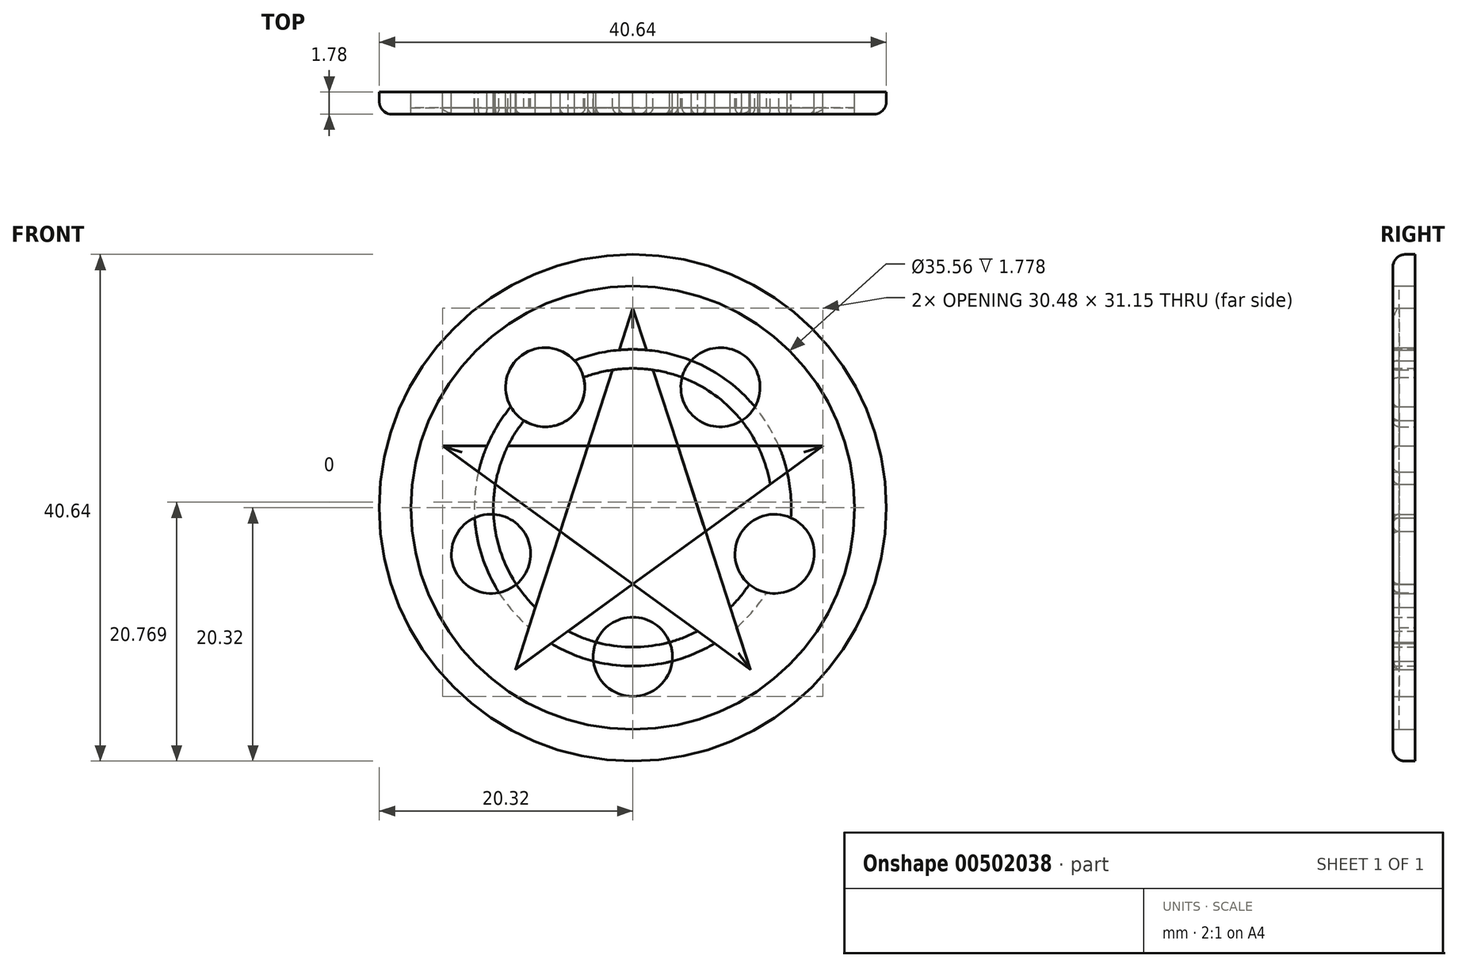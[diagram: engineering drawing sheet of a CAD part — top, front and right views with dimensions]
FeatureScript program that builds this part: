
annotation { "Feature Type Name" : "Feature", "Feature Type Description" : "" }
export const myFeature = defineFeature(function(context is Context, id is Id, definition is map)
    precondition{}
    {
        {
            var Q0;
            Q0=qCreatedBy(makeId("Front.planeOp"),FACE);
            var sketch = newSketch(context, id + "F0", { "sketchPlane" : qUnion([Q0])});
            skCircle(sketch, "E0", {"center": v(0, 0) * mm, "radius": 20.32 * mm});
            skCircle(sketch, "E1", {"center": v(0, 0) * mm, "radius": 17.78 * mm});
            skLineSegment(sketch, "E2", {"start": v(0, 16.02) * mm, "end": v(-9.42, -12.96) * mm});
            skLineSegment(sketch, "E3", {"start": v(-9.42, -12.96) * mm, "end": v(15.24, 4.95) * mm});
            skLineSegment(sketch, "E4", {"start": v(-15.24, 4.95) * mm, "end": v(15.24, 4.95) * mm});
            skLineSegment(sketch, "E5", {"start": v(0, 16.02) * mm, "end": v(9.42, -12.96) * mm});
            skLineSegment(sketch, "E6", {"start": v(9.42, -12.96) * mm, "end": v(-15.24, 4.95) * mm});
            skPoint(sketch, "E7", {"position": v(3.6, 4.95) * mm});
            skPoint(sketch, "E8", {"position": v(-3.6, 4.95) * mm});
            skPoint(sketch, "E9", {"position": v(-5.82, -1.9) * mm});
            skPoint(sketch, "E10", {"position": v(0, -6.12) * mm});
            skPoint(sketch, "E11", {"position": v(5.82, -1.9) * mm});
            skPoint(sketch, "E12", {"position": v(-7.02, 9.67) * mm});
            skPoint(sketch, "E13", {"position": v(7.02, 9.67) * mm});
            skPoint(sketch, "E14", {"position": v(11.37, -3.7) * mm});
            skPoint(sketch, "E15", {"position": v(0, -11.95) * mm});
            skPoint(sketch, "E16", {"position": v(-11.37, -3.7) * mm});
            skPoint(sketch, "E17.orphan", {"position": v(-10.45, 14.38) * mm});
            skPoint(sketch, "E18.end.orphan", {"position": v(10.45, 14.38) * mm});
            skPoint(sketch, "E19.end.orphan", {"position": v(16.9, -5.5) * mm});
            skPoint(sketch, "E20.end.orphan", {"position": v(0, -17.78) * mm});
            skPoint(sketch, "E21.end.orphan", {"position": v(-16.9, -5.5) * mm});
            skCircle(sketch, "E22", {"center": v(-7.02, 9.67) * mm, "radius": 3.18 * mm});
            skCircle(sketch, "E23", {"center": v(-11.37, -3.7) * mm, "radius": 3.18 * mm});
            skCircle(sketch, "E24", {"center": v(0, -11.95) * mm, "radius": 3.18 * mm});
            skCircle(sketch, "E25", {"center": v(11.37, -3.7) * mm, "radius": 3.18 * mm});
            skCircle(sketch, "E26", {"center": v(7.02, 9.67) * mm, "radius": 3.18 * mm});
            skCircle(sketch, "E27", {"center": v(0, 0) * mm, "radius": 12.7 * mm});
            skCircle(sketch, "E28", {"center": v(0, 0) * mm, "radius": 11.18 * mm});
            skSolve(sketch);
        }
        {
            var Q0;
            Q0=makeQuery(id+"F0.imprint","IMPRINT",FACE,{"disambiguationData":[TD([[makeQuery(id+"F0.imprint","IMPRINT",EDGE,{"derivedFrom":sQuery(id+"F0.wireOp",EDGE,"E0")}),1.0]])]});
            var Q1;
            {var subQ0=sQuery(id+"F0.wireOp",EDGE,"E4");var subQ1=sQuery(id+"F0.wireOp",EDGE,"E2");var subQ2=makeQuery(id+"F0.imprint","INTERSECT",VERTEX,{"derivedFrom":[subQ1,subQ0]});Q1=makeQuery(id+"F0.imprint","IMPRINT",FACE,{"disambiguationData":[TD([[makeQuery(id+"F0.imprint","IMPRINT",EDGE,{"disambiguationData":[TD([[subQ2,-1.0]])],"derivedFrom":subQ1}),-1.0]])]});}
            var Q2;
            {var subQ0=sQuery(id+"F0.wireOp",EDGE,"E5");var subQ1=sQuery(id+"F0.wireOp",EDGE,"E2");var subQ2=makeQuery(id+"F0.imprint","INTERSECT",VERTEX,{"derivedFrom":[subQ1,subQ0]});Q2=makeQuery(id+"F0.imprint","IMPRINT",FACE,{"disambiguationData":[TD([[makeQuery(id+"F0.imprint","IMPRINT",EDGE,{"disambiguationData":[TD([[subQ2,-1.0]])],"derivedFrom":subQ1}),1.0]])]});}
            var Q3;
            {var subQ0=sQuery(id+"F0.wireOp",EDGE,"E4");var subQ1=sQuery(id+"F0.wireOp",EDGE,"E3");var subQ2=makeQuery(id+"F0.imprint","INTERSECT",VERTEX,{"derivedFrom":[subQ1,subQ0]});Q3=makeQuery(id+"F0.imprint","IMPRINT",FACE,{"disambiguationData":[TD([[makeQuery(id+"F0.imprint","IMPRINT",EDGE,{"disambiguationData":[TD([[subQ2,1.0]])],"derivedFrom":subQ1}),1.0]])]});}
            var Q4;
            {var subQ0=sQuery(id+"F0.wireOp",EDGE,"E6");var subQ1=sQuery(id+"F0.wireOp",EDGE,"E3");var subQ2=makeQuery(id+"F0.imprint","INTERSECT",VERTEX,{"derivedFrom":[subQ1,subQ0]});Q4=makeQuery(id+"F0.imprint","IMPRINT",FACE,{"disambiguationData":[TD([[makeQuery(id+"F0.imprint","IMPRINT",EDGE,{"disambiguationData":[TD([[subQ2,-1.0]])],"derivedFrom":subQ1}),-1.0]])]});}
            var Q5;
            {var subQ0=sQuery(id+"F0.wireOp",EDGE,"E3");var subQ1=sQuery(id+"F0.wireOp",EDGE,"E2");var subQ2=makeQuery(id+"F0.imprint","INTERSECT",VERTEX,{"derivedFrom":[subQ1,subQ0]});Q5=makeQuery(id+"F0.imprint","IMPRINT",FACE,{"disambiguationData":[TD([[makeQuery(id+"F0.imprint","IMPRINT",EDGE,{"disambiguationData":[TD([[subQ2,1.0]])],"derivedFrom":subQ1}),1.0]])]});}
            var Q6;
            Q6=makeQuery(id+"F0.imprint","IMPRINT",FACE,{"disambiguationData":[TD([[makeQuery(id+"F0.imprint","IMPRINT",EDGE,{"derivedFrom":sQuery(id+"F0.wireOp",EDGE,"E23")}),1.0]])]});
            var Q7;
            Q7=makeQuery(id+"F0.imprint","IMPRINT",FACE,{"disambiguationData":[TD([[makeQuery(id+"F0.imprint","IMPRINT",EDGE,{"derivedFrom":sQuery(id+"F0.wireOp",EDGE,"E22")}),1.0]])]});
            var Q8;
            Q8=makeQuery(id+"F0.imprint","IMPRINT",FACE,{"disambiguationData":[TD([[makeQuery(id+"F0.imprint","IMPRINT",EDGE,{"derivedFrom":sQuery(id+"F0.wireOp",EDGE,"E26")}),1.0]])]});
            var Q9;
            Q9=makeQuery(id+"F0.imprint","IMPRINT",FACE,{"disambiguationData":[TD([[makeQuery(id+"F0.imprint","IMPRINT",EDGE,{"derivedFrom":sQuery(id+"F0.wireOp",EDGE,"E25")}),1.0]])]});
            var Q10;
            Q10=makeQuery(id+"F0.imprint","IMPRINT",FACE,{"disambiguationData":[TD([[makeQuery(id+"F0.imprint","IMPRINT",EDGE,{"derivedFrom":sQuery(id+"F0.wireOp",EDGE,"E24")}),1.0]])]});
            var Q11;
            {var subQ0=sQuery(id+"F0.wireOp",EDGE,"E28");var subQ1=sQuery(id+"F0.wireOp",EDGE,"E2");var subQ2=makeQuery(id+"F0.imprint","INTERSECT",VERTEX,{"disambiguationData":[OD(0.0)],"derivedFrom":[subQ1,subQ0]});Q11=makeQuery(id+"F0.imprint","IMPRINT",FACE,{"disambiguationData":[TD([[makeQuery(id+"F0.imprint","IMPRINT",EDGE,{"disambiguationData":[TD([[subQ2,-1.0]])],"derivedFrom":subQ1}),1.0]])]});}
            var Q12;
            {var subQ0=sQuery(id+"F0.wireOp",EDGE,"E27");var subQ1=sQuery(id+"F0.wireOp",EDGE,"E2");var subQ2=makeQuery(id+"F0.imprint","INTERSECT",VERTEX,{"disambiguationData":[OD(0.0)],"derivedFrom":[subQ1,subQ0]});Q12=makeQuery(id+"F0.imprint","IMPRINT",FACE,{"disambiguationData":[TD([[makeQuery(id+"F0.imprint","IMPRINT",EDGE,{"disambiguationData":[TD([[subQ2,-1.0]])],"derivedFrom":subQ1}),1.0]])]});}
            var Q13;
            {var subQ0=sQuery(id+"F0.wireOp",EDGE,"E5");var subQ1=sQuery(id+"F0.wireOp",EDGE,"E3");var subQ2=makeQuery(id+"F0.imprint","INTERSECT",VERTEX,{"derivedFrom":[subQ1,subQ0]});Q13=makeQuery(id+"F0.imprint","IMPRINT",FACE,{"disambiguationData":[TD([[makeQuery(id+"F0.imprint","IMPRINT",EDGE,{"disambiguationData":[TD([[subQ2,-1.0]])],"derivedFrom":subQ1}),1.0]])]});}
            var Q14;
            {var subQ0=sQuery(id+"F0.wireOp",EDGE,"E28");var subQ1=sQuery(id+"F0.wireOp",EDGE,"E3");var subQ2=makeQuery(id+"F0.imprint","INTERSECT",VERTEX,{"disambiguationData":[OD(1.0)],"derivedFrom":[subQ1,subQ0]});Q14=makeQuery(id+"F0.imprint","IMPRINT",FACE,{"disambiguationData":[TD([[makeQuery(id+"F0.imprint","IMPRINT",EDGE,{"disambiguationData":[TD([[subQ2,-1.0]])],"derivedFrom":subQ1}),1.0]])]});}
            var Q15;
            {var subQ0=sQuery(id+"F0.wireOp",EDGE,"E6");var subQ1=sQuery(id+"F0.wireOp",EDGE,"E5");var subQ2=makeQuery(id+"F0.imprint","INTERSECT",VERTEX,{"derivedFrom":[subQ1,subQ0]});Q15=makeQuery(id+"F0.imprint","IMPRINT",FACE,{"disambiguationData":[TD([[makeQuery(id+"F0.imprint","IMPRINT",EDGE,{"disambiguationData":[TD([[subQ2,1.0]])],"derivedFrom":subQ1}),-1.0]])]});}
            var Q16;
            {var subQ0=sQuery(id+"F0.wireOp",EDGE,"E28");var subQ1=sQuery(id+"F0.wireOp",EDGE,"E5");var subQ2=makeQuery(id+"F0.imprint","INTERSECT",VERTEX,{"disambiguationData":[OD(1.0)],"derivedFrom":[subQ1,subQ0]});Q16=makeQuery(id+"F0.imprint","IMPRINT",FACE,{"disambiguationData":[TD([[makeQuery(id+"F0.imprint","IMPRINT",EDGE,{"disambiguationData":[TD([[subQ2,-1.0]])],"derivedFrom":subQ1}),-1.0]])]});}
            var Q17;
            {var subQ0=sQuery(id+"F0.wireOp",EDGE,"E28");var subQ1=sQuery(id+"F0.wireOp",EDGE,"E2");var subQ2=makeQuery(id+"F0.imprint","INTERSECT",VERTEX,{"disambiguationData":[OD(1.0)],"derivedFrom":[subQ1,subQ0]});Q17=makeQuery(id+"F0.imprint","IMPRINT",FACE,{"disambiguationData":[TD([[makeQuery(id+"F0.imprint","IMPRINT",EDGE,{"disambiguationData":[TD([[subQ2,-1.0]])],"derivedFrom":subQ1}),1.0]])]});}
            var Q18;
            {var subQ0=sQuery(id+"F0.wireOp",EDGE,"E6");var subQ1=sQuery(id+"F0.wireOp",EDGE,"E2");var subQ2=makeQuery(id+"F0.imprint","INTERSECT",VERTEX,{"derivedFrom":[subQ1,subQ0]});Q18=makeQuery(id+"F0.imprint","IMPRINT",FACE,{"disambiguationData":[TD([[makeQuery(id+"F0.imprint","IMPRINT",EDGE,{"disambiguationData":[TD([[subQ2,-1.0]])],"derivedFrom":subQ1}),1.0]])]});}
            var Q19;
            {var subQ0=sQuery(id+"F0.wireOp",EDGE,"E28");var subQ1=sQuery(id+"F0.wireOp",EDGE,"E26");var subQ2=makeQuery(id+"F0.imprint","INTERSECT",VERTEX,{"disambiguationData":[OD(0.0)],"derivedFrom":[subQ1,subQ0]});Q19=makeQuery(id+"F0.imprint","IMPRINT",FACE,{"disambiguationData":[TD([[makeQuery(id+"F0.imprint","IMPRINT",EDGE,{"disambiguationData":[TD([[subQ2,-1.0]])],"derivedFrom":subQ1}),1.0]])]});}
            var Q20;
            {var subQ0=sQuery(id+"F0.wireOp",EDGE,"E27");var subQ1=sQuery(id+"F0.wireOp",EDGE,"E26");var subQ2=makeQuery(id+"F0.imprint","INTERSECT",VERTEX,{"disambiguationData":[OD(0.0)],"derivedFrom":[subQ1,subQ0]});Q20=makeQuery(id+"F0.imprint","IMPRINT",FACE,{"disambiguationData":[TD([[makeQuery(id+"F0.imprint","IMPRINT",EDGE,{"disambiguationData":[TD([[subQ2,1.0]])],"derivedFrom":subQ1}),1.0]])]});}
            var Q21;
            {var subQ0=sQuery(id+"F0.wireOp",EDGE,"E27");var subQ1=sQuery(id+"F0.wireOp",EDGE,"E22");var subQ2=makeQuery(id+"F0.imprint","INTERSECT",VERTEX,{"disambiguationData":[OD(0.0)],"derivedFrom":[subQ1,subQ0]});Q21=makeQuery(id+"F0.imprint","IMPRINT",FACE,{"disambiguationData":[TD([[makeQuery(id+"F0.imprint","IMPRINT",EDGE,{"disambiguationData":[TD([[subQ2,-1.0]])],"derivedFrom":subQ1}),1.0]])]});}
            var Q22;
            {var subQ0=sQuery(id+"F0.wireOp",EDGE,"E28");var subQ1=sQuery(id+"F0.wireOp",EDGE,"E22");var subQ2=makeQuery(id+"F0.imprint","INTERSECT",VERTEX,{"disambiguationData":[OD(0.0)],"derivedFrom":[subQ1,subQ0]});Q22=makeQuery(id+"F0.imprint","IMPRINT",FACE,{"disambiguationData":[TD([[makeQuery(id+"F0.imprint","IMPRINT",EDGE,{"disambiguationData":[TD([[subQ2,1.0]])],"derivedFrom":subQ1}),1.0]])]});}
            var Q23;
            {var subQ0=sQuery(id+"F0.wireOp",EDGE,"E28");var subQ1=sQuery(id+"F0.wireOp",EDGE,"E23");var subQ2=makeQuery(id+"F0.imprint","INTERSECT",VERTEX,{"disambiguationData":[OD(0.0)],"derivedFrom":[subQ1,subQ0]});Q23=makeQuery(id+"F0.imprint","IMPRINT",FACE,{"disambiguationData":[TD([[makeQuery(id+"F0.imprint","IMPRINT",EDGE,{"disambiguationData":[TD([[subQ2,1.0]])],"derivedFrom":subQ1}),1.0]])]});}
            var Q24;
            {var subQ0=sQuery(id+"F0.wireOp",EDGE,"E27");var subQ1=sQuery(id+"F0.wireOp",EDGE,"E23");var subQ2=makeQuery(id+"F0.imprint","INTERSECT",VERTEX,{"disambiguationData":[OD(0.0)],"derivedFrom":[subQ1,subQ0]});Q24=makeQuery(id+"F0.imprint","IMPRINT",FACE,{"disambiguationData":[TD([[makeQuery(id+"F0.imprint","IMPRINT",EDGE,{"disambiguationData":[TD([[subQ2,-1.0]])],"derivedFrom":subQ1}),1.0]])]});}
            var Q25;
            {var subQ0=sQuery(id+"F0.wireOp",EDGE,"E27");var subQ1=sQuery(id+"F0.wireOp",EDGE,"E4");var subQ2=makeQuery(id+"F0.imprint","INTERSECT",VERTEX,{"disambiguationData":[OD(0.0)],"derivedFrom":[subQ1,subQ0]});Q25=makeQuery(id+"F0.imprint","IMPRINT",FACE,{"disambiguationData":[TD([[makeQuery(id+"F0.imprint","IMPRINT",EDGE,{"disambiguationData":[TD([[subQ2,-1.0]])],"derivedFrom":subQ1}),-1.0]])]});}
            var Q26;
            {var subQ0=sQuery(id+"F0.wireOp",EDGE,"E6");var subQ1=sQuery(id+"F0.wireOp",EDGE,"E4");var subQ2=makeQuery(id+"F0.imprint","INTERSECT",VERTEX,{"derivedFrom":[subQ1,subQ0]});Q26=makeQuery(id+"F0.imprint","IMPRINT",FACE,{"disambiguationData":[TD([[makeQuery(id+"F0.imprint","IMPRINT",EDGE,{"disambiguationData":[TD([[subQ2,-1.0]])],"derivedFrom":subQ1}),-1.0]])]});}
            var Q27;
            {var subQ0=sQuery(id+"F0.wireOp",EDGE,"E28");var subQ1=sQuery(id+"F0.wireOp",EDGE,"E24");var subQ2=makeQuery(id+"F0.imprint","INTERSECT",VERTEX,{"disambiguationData":[OD(0.0)],"derivedFrom":[subQ1,subQ0]});Q27=makeQuery(id+"F0.imprint","IMPRINT",FACE,{"disambiguationData":[TD([[makeQuery(id+"F0.imprint","IMPRINT",EDGE,{"disambiguationData":[TD([[subQ2,1.0]])],"derivedFrom":subQ1}),1.0]])]});}
            var Q28;
            {var subQ0=sQuery(id+"F0.wireOp",EDGE,"E27");var subQ1=sQuery(id+"F0.wireOp",EDGE,"E24");var subQ2=makeQuery(id+"F0.imprint","INTERSECT",VERTEX,{"disambiguationData":[OD(0.0)],"derivedFrom":[subQ1,subQ0]});Q28=makeQuery(id+"F0.imprint","IMPRINT",FACE,{"disambiguationData":[TD([[makeQuery(id+"F0.imprint","IMPRINT",EDGE,{"disambiguationData":[TD([[subQ2,-1.0]])],"derivedFrom":subQ1}),1.0]])]});}
            var Q29;
            {var subQ0=sQuery(id+"F0.wireOp",EDGE,"E28");var subQ1=sQuery(id+"F0.wireOp",EDGE,"E25");var subQ2=makeQuery(id+"F0.imprint","INTERSECT",VERTEX,{"disambiguationData":[OD(0.0)],"derivedFrom":[subQ1,subQ0]});Q29=makeQuery(id+"F0.imprint","IMPRINT",FACE,{"disambiguationData":[TD([[makeQuery(id+"F0.imprint","IMPRINT",EDGE,{"disambiguationData":[TD([[subQ2,-1.0]])],"derivedFrom":subQ1}),1.0]])]});}
            var Q30;
            {var subQ0=sQuery(id+"F0.wireOp",EDGE,"E27");var subQ1=sQuery(id+"F0.wireOp",EDGE,"E25");var subQ2=makeQuery(id+"F0.imprint","INTERSECT",VERTEX,{"disambiguationData":[OD(0.0)],"derivedFrom":[subQ1,subQ0]});Q30=makeQuery(id+"F0.imprint","IMPRINT",FACE,{"disambiguationData":[TD([[makeQuery(id+"F0.imprint","IMPRINT",EDGE,{"disambiguationData":[TD([[subQ2,1.0]])],"derivedFrom":subQ1}),1.0]])]});}
            extrude(context, id + "F1", {"entities" : qUnion([Q0, Q1, Q2, Q3, Q4, Q5, Q6, Q7, Q8, Q9, Q10, Q11, Q12, Q13, Q14, Q15, Q16, Q17, Q18, Q19, Q20, Q21, Q22, Q23, Q24, Q25, Q26, Q27, Q28, Q29, Q30]), "depth" : 1.78 * mm, "offsetDistance" : 25.4 * mm});
        }
        {
            var Q0;
            Q0=makeQuery(id+"F1.opExtrude","CAP_EDGE",EDGE,{"disambiguationData":[OSD([sQuery(id+"F0.wireOp",EDGE,"E0")])],"isStart":false});
            fillet(context, id + "F2", {"entities" : qUnion([Q0]), "radius" : 1 * mm, "tangentPropagation" : true, "allowEdgeOverflow" : false});
        }
        {
            var Q0;
            {var subQ3=sQuery(id+"F0.wireOp",EDGE,"E4");var subQ5=sQuery(id+"F0.wireOp",EDGE,"E2");var subQ6=makeQuery(id+"F0.imprint","INTERSECT",VERTEX,{"derivedFrom":[subQ5,subQ3]});Q0=makeQuery(id+"F0.imprint","IMPRINT",FACE,{"disambiguationData":[TD([[makeQuery(id+"F0.imprint","IMPRINT",EDGE,{"disambiguationData":[TD([[subQ6,-1.0]])],"derivedFrom":subQ5}),1.0]])]});}
            extrude(context, id + "F3", {"entities" : qUnion([Q0]), "depth" : 1.78 * mm, "offsetDistance" : 25.4 * mm});
        }
        {
            var Q0;
            Q0=makeQuery(id+"F0.imprint","IMPRINT",FACE,{"disambiguationData":[TD([[makeQuery(id+"F0.imprint","IMPRINT",EDGE,{"derivedFrom":sQuery(id+"F0.wireOp",EDGE,"E1")}),1.0]])]});
            var Q1;
            {var subQ4=sQuery(id+"F0.wireOp",EDGE,"E2");var subQ6=sQuery(id+"F0.wireOp",EDGE,"E6");var subQ7=makeQuery(id+"F0.imprint","INTERSECT",VERTEX,{"derivedFrom":[subQ4,subQ6]});Q1=makeQuery(id+"F0.imprint","IMPRINT",FACE,{"disambiguationData":[TD([[makeQuery(id+"F0.imprint","IMPRINT",EDGE,{"disambiguationData":[TD([[subQ7,-1.0]])],"derivedFrom":subQ4}),-1.0]])]});}
            var Q2;
            {var subQ0=sQuery(id+"F0.wireOp",EDGE,"E28");var subQ1=sQuery(id+"F0.wireOp",EDGE,"E2");var subQ2=makeQuery(id+"F0.imprint","INTERSECT",VERTEX,{"disambiguationData":[OD(0.0)],"derivedFrom":[subQ1,subQ0]});Q2=makeQuery(id+"F0.imprint","IMPRINT",FACE,{"disambiguationData":[TD([[makeQuery(id+"F0.imprint","IMPRINT",EDGE,{"disambiguationData":[TD([[subQ2,-1.0]])],"derivedFrom":subQ1}),-1.0]])]});}
            var Q3;
            {var subQ1=sQuery(id+"F0.wireOp",EDGE,"E4");var subQ6=sQuery(id+"F0.wireOp",EDGE,"E5");var subQ7=makeQuery(id+"F0.imprint","INTERSECT",VERTEX,{"derivedFrom":[subQ1,subQ6]});Q3=makeQuery(id+"F0.imprint","IMPRINT",FACE,{"disambiguationData":[TD([[makeQuery(id+"F0.imprint","IMPRINT",EDGE,{"disambiguationData":[TD([[subQ7,-1.0]])],"derivedFrom":subQ1}),1.0]])]});}
            var Q4;
            {var subQ1=sQuery(id+"F0.wireOp",EDGE,"E5");var subQ6=sQuery(id+"F0.wireOp",EDGE,"E3");var subQ7=makeQuery(id+"F0.imprint","INTERSECT",VERTEX,{"derivedFrom":[subQ6,subQ1]});Q4=makeQuery(id+"F0.imprint","IMPRINT",FACE,{"disambiguationData":[TD([[makeQuery(id+"F0.imprint","IMPRINT",EDGE,{"disambiguationData":[TD([[subQ7,-1.0]])],"derivedFrom":subQ6}),-1.0]])]});}
            var Q5;
            {var subQ0=sQuery(id+"F0.wireOp",EDGE,"E28");var subQ1=sQuery(id+"F0.wireOp",EDGE,"E3");var subQ2=makeQuery(id+"F0.imprint","INTERSECT",VERTEX,{"disambiguationData":[OD(0.0)],"derivedFrom":[subQ1,subQ0]});Q5=makeQuery(id+"F0.imprint","IMPRINT",FACE,{"disambiguationData":[TD([[makeQuery(id+"F0.imprint","IMPRINT",EDGE,{"disambiguationData":[TD([[subQ2,-1.0]])],"derivedFrom":subQ1}),-1.0]])]});}
            extrude(context, id + "F4", {"entities" : qUnion([Q0, Q1, Q2, Q3, Q4, Q5]), "depth" : 1.27 * mm, "offsetDistance" : 25.4 * mm});
        }
        {
            var Q0;
            {var subQ0=sQuery(id+"F0.wireOp",EDGE,"E27");var subQ1=sQuery(id+"F0.wireOp",EDGE,"E5");var subQ2=makeQuery(id+"F0.imprint","INTERSECT",VERTEX,{"disambiguationData":[OD(0.0)],"derivedFrom":[subQ1,subQ0]});Q0=makeQuery(id+"F0.imprint","IMPRINT",FACE,{"disambiguationData":[TD([[makeQuery(id+"F0.imprint","IMPRINT",EDGE,{"disambiguationData":[TD([[subQ2,-1.0]])],"derivedFrom":subQ1}),1.0]])]});}
            var Q1;
            {var subQ0=sQuery(id+"F0.wireOp",EDGE,"E28");var subQ1=sQuery(id+"F0.wireOp",EDGE,"E4");var subQ2=makeQuery(id+"F0.imprint","INTERSECT",VERTEX,{"disambiguationData":[OD(1.0)],"derivedFrom":[subQ1,subQ0]});Q1=makeQuery(id+"F0.imprint","IMPRINT",FACE,{"disambiguationData":[TD([[makeQuery(id+"F0.imprint","IMPRINT",EDGE,{"disambiguationData":[TD([[subQ2,-1.0]])],"derivedFrom":subQ1}),1.0]])]});}
            var Q2;
            {var subQ0=sQuery(id+"F0.wireOp",EDGE,"E28");var subQ1=sQuery(id+"F0.wireOp",EDGE,"E3");var subQ2=makeQuery(id+"F0.imprint","INTERSECT",VERTEX,{"disambiguationData":[OD(1.0)],"derivedFrom":[subQ1,subQ0]});Q2=makeQuery(id+"F0.imprint","IMPRINT",FACE,{"disambiguationData":[TD([[makeQuery(id+"F0.imprint","IMPRINT",EDGE,{"disambiguationData":[TD([[subQ2,-1.0]])],"derivedFrom":subQ1}),-1.0]])]});}
            var Q3;
            {var subQ0=sQuery(id+"F0.wireOp",EDGE,"E28");var subQ1=sQuery(id+"F0.wireOp",EDGE,"E5");var subQ2=makeQuery(id+"F0.imprint","INTERSECT",VERTEX,{"disambiguationData":[OD(1.0)],"derivedFrom":[subQ1,subQ0]});Q3=makeQuery(id+"F0.imprint","IMPRINT",FACE,{"disambiguationData":[TD([[makeQuery(id+"F0.imprint","IMPRINT",EDGE,{"disambiguationData":[TD([[subQ2,-1.0]])],"derivedFrom":subQ1}),1.0]])]});}
            var Q4;
            {var subQ0=sQuery(id+"F0.wireOp",EDGE,"E27");var subQ1=sQuery(id+"F0.wireOp",EDGE,"E6");var subQ2=makeQuery(id+"F0.imprint","INTERSECT",VERTEX,{"disambiguationData":[OD(0.0)],"derivedFrom":[subQ1,subQ0]});Q4=makeQuery(id+"F0.imprint","IMPRINT",FACE,{"disambiguationData":[TD([[makeQuery(id+"F0.imprint","IMPRINT",EDGE,{"disambiguationData":[TD([[subQ2,-1.0]])],"derivedFrom":subQ1}),1.0]])]});}
            var Q5;
            {var subQ0=sQuery(id+"F0.wireOp",EDGE,"E27");var subQ1=sQuery(id+"F0.wireOp",EDGE,"E3");var subQ2=makeQuery(id+"F0.imprint","INTERSECT",VERTEX,{"disambiguationData":[OD(0.0)],"derivedFrom":[subQ1,subQ0]});Q5=makeQuery(id+"F0.imprint","IMPRINT",FACE,{"disambiguationData":[TD([[makeQuery(id+"F0.imprint","IMPRINT",EDGE,{"disambiguationData":[TD([[subQ2,-1.0]])],"derivedFrom":subQ1}),-1.0]])]});}
            var Q6;
            {var subQ0=sQuery(id+"F0.wireOp",EDGE,"E28");var subQ1=sQuery(id+"F0.wireOp",EDGE,"E2");var subQ2=makeQuery(id+"F0.imprint","INTERSECT",VERTEX,{"disambiguationData":[OD(1.0)],"derivedFrom":[subQ1,subQ0]});Q6=makeQuery(id+"F0.imprint","IMPRINT",FACE,{"disambiguationData":[TD([[makeQuery(id+"F0.imprint","IMPRINT",EDGE,{"disambiguationData":[TD([[subQ2,-1.0]])],"derivedFrom":subQ1}),-1.0]])]});}
            var Q7;
            {var subQ0=sQuery(id+"F0.wireOp",EDGE,"E28");var subQ1=sQuery(id+"F0.wireOp",EDGE,"E6");var subQ2=makeQuery(id+"F0.imprint","INTERSECT",VERTEX,{"disambiguationData":[OD(1.0)],"derivedFrom":[subQ1,subQ0]});Q7=makeQuery(id+"F0.imprint","IMPRINT",FACE,{"disambiguationData":[TD([[makeQuery(id+"F0.imprint","IMPRINT",EDGE,{"disambiguationData":[TD([[subQ2,-1.0]])],"derivedFrom":subQ1}),1.0]])]});}
            var Q8;
            {var subQ0=sQuery(id+"F0.wireOp",EDGE,"E27");var subQ1=sQuery(id+"F0.wireOp",EDGE,"E4");var subQ2=makeQuery(id+"F0.imprint","INTERSECT",VERTEX,{"disambiguationData":[OD(0.0)],"derivedFrom":[subQ1,subQ0]});Q8=makeQuery(id+"F0.imprint","IMPRINT",FACE,{"disambiguationData":[TD([[makeQuery(id+"F0.imprint","IMPRINT",EDGE,{"disambiguationData":[TD([[subQ2,-1.0]])],"derivedFrom":subQ1}),1.0]])]});}
            var Q9;
            {var subQ0=sQuery(id+"F0.wireOp",EDGE,"E27");var subQ1=sQuery(id+"F0.wireOp",EDGE,"E2");var subQ2=makeQuery(id+"F0.imprint","INTERSECT",VERTEX,{"disambiguationData":[OD(0.0)],"derivedFrom":[subQ1,subQ0]});Q9=makeQuery(id+"F0.imprint","IMPRINT",FACE,{"disambiguationData":[TD([[makeQuery(id+"F0.imprint","IMPRINT",EDGE,{"disambiguationData":[TD([[subQ2,-1.0]])],"derivedFrom":subQ1}),-1.0]])]});}
            extrude(context, id + "F5", {"entities" : qUnion([Q0, Q1, Q2, Q3, Q4, Q5, Q6, Q7, Q8, Q9]), "depth" : 1.78 * mm, "offsetDistance" : 25.4 * mm});
        }
        {
            var Q0;
            Q0=makeQuery(id+"F1.opExtrude","CAP_EDGE",EDGE,{"disambiguationData":[OSD([sQuery(id+"F0.wireOp",EDGE,"E22")])],"isStart":false});
            var Q1;
            Q1=makeQuery(id+"F1.opExtrude","CAP_EDGE",EDGE,{"disambiguationData":[OSD([sQuery(id+"F0.wireOp",EDGE,"E23")])],"isStart":false});
            var Q2;
            Q2=makeQuery(id+"F1.opExtrude","CAP_EDGE",EDGE,{"disambiguationData":[OSD([sQuery(id+"F0.wireOp",EDGE,"E24")])],"isStart":false});
            var Q3;
            Q3=makeQuery(id+"F1.opExtrude","CAP_EDGE",EDGE,{"disambiguationData":[OSD([sQuery(id+"F0.wireOp",EDGE,"E25")])],"isStart":false});
            var Q4;
            Q4=makeQuery(id+"F1.opExtrude","CAP_EDGE",EDGE,{"disambiguationData":[OSD([sQuery(id+"F0.wireOp",EDGE,"E26")])],"isStart":false});
            var Q5;
            {var subQ0=sQuery(id+"F0.wireOp",EDGE,"E4");var subQ2=makeQuery(id+"F0.imprint","INTERSECT",VERTEX,{"disambiguationData":[OD(0.0)],"derivedFrom":[subQ0,sQuery(id+"F0.wireOp",EDGE,"E27")]});Q5=makeQuery(id+"F1.opExtrude","CAP_EDGE",EDGE,{"disambiguationData":[OSD([subQ0]),TDD([makeQuery(id+"F0.imprint","IMPRINT",EDGE,{"disambiguationData":[TD([[makeQuery(id+"F0.imprint","INTERSECT",VERTEX,{"derivedFrom":[subQ0,sQuery(id+"F0.wireOp",EDGE,"E6")]}),-1.0]])],"derivedFrom":subQ0}),makeQuery(id+"F0.imprint","IMPRINT",EDGE,{"disambiguationData":[TD([[subQ2,-1.0]])],"derivedFrom":subQ0}),makeQuery(id+"F0.imprint","IMPRINT",EDGE,{"disambiguationData":[TD([[makeQuery(id+"F0.imprint","INTERSECT",VERTEX,{"derivedFrom":[sQuery(id+"F0.wireOp",EDGE,"E2"),subQ0]}),1.0]])],"derivedFrom":subQ0})])],"isStart":false});}
            var Q6;
            {var subQ0=sQuery(id+"F0.wireOp",EDGE,"E6");var subQ2=makeQuery(id+"F0.imprint","INTERSECT",VERTEX,{"disambiguationData":[OD(1.0)],"derivedFrom":[subQ0,sQuery(id+"F0.wireOp",EDGE,"E28")]});Q6=makeQuery(id+"F1.opExtrude","CAP_EDGE",EDGE,{"disambiguationData":[OSD([subQ0]),TDD([makeQuery(id+"F0.imprint","IMPRINT",EDGE,{"disambiguationData":[TD([[makeQuery(id+"F0.imprint","INTERSECT",VERTEX,{"derivedFrom":[sQuery(id+"F0.wireOp",EDGE,"E2"),subQ0]}),-1.0]])],"derivedFrom":subQ0}),makeQuery(id+"F0.imprint","IMPRINT",EDGE,{"disambiguationData":[TD([[subQ2,-1.0]])],"derivedFrom":subQ0}),makeQuery(id+"F0.imprint","IMPRINT",EDGE,{"disambiguationData":[TD([[makeQuery(id+"F0.imprint","INTERSECT",VERTEX,{"derivedFrom":[sQuery(id+"F0.wireOp",EDGE,"E4"),subQ0]}),1.0]])],"derivedFrom":subQ0})])],"isStart":false});}
            var Q7;
            {var subQ0=sQuery(id+"F0.wireOp",EDGE,"E2");var subQ1=makeQuery(id+"F0.imprint","INTERSECT",VERTEX,{"disambiguationData":[OD(0.0)],"derivedFrom":[subQ0,sQuery(id+"F0.wireOp",EDGE,"E28")]});var subQ2=makeQuery(id+"F0.imprint","INTERSECT",VERTEX,{"disambiguationData":[OD(0.0)],"derivedFrom":[subQ0,sQuery(id+"F0.wireOp",EDGE,"E27")]});Q7=makeQuery(id+"F1.opExtrude","CAP_EDGE",EDGE,{"disambiguationData":[OSD([subQ0]),TDD([makeQuery(id+"F0.imprint","IMPRINT",EDGE,{"disambiguationData":[TD([[makeQuery(id+"F0.imprint","INTERSECT",VERTEX,{"derivedFrom":[subQ0,sQuery(id+"F0.wireOp",EDGE,"E5")]}),-1.0]])],"derivedFrom":subQ0}),makeQuery(id+"F0.imprint","IMPRINT",EDGE,{"disambiguationData":[TD([[subQ2,-1.0]])],"derivedFrom":subQ0}),makeQuery(id+"F0.imprint","IMPRINT",EDGE,{"disambiguationData":[TD([[subQ1,-1.0]])],"derivedFrom":subQ0})])],"isStart":false});}
            var Q8;
            {var subQ0=sQuery(id+"F0.wireOp",EDGE,"E5");var subQ2=makeQuery(id+"F0.imprint","INTERSECT",VERTEX,{"disambiguationData":[OD(0.0)],"derivedFrom":[subQ0,sQuery(id+"F0.wireOp",EDGE,"E27")]});Q8=makeQuery(id+"F1.opExtrude","CAP_EDGE",EDGE,{"disambiguationData":[OSD([subQ0]),TDD([makeQuery(id+"F0.imprint","IMPRINT",EDGE,{"disambiguationData":[TD([[makeQuery(id+"F0.imprint","INTERSECT",VERTEX,{"derivedFrom":[sQuery(id+"F0.wireOp",EDGE,"E2"),subQ0]}),-1.0]])],"derivedFrom":subQ0}),makeQuery(id+"F0.imprint","IMPRINT",EDGE,{"disambiguationData":[TD([[subQ2,-1.0]])],"derivedFrom":subQ0}),makeQuery(id+"F0.imprint","IMPRINT",EDGE,{"disambiguationData":[TD([[makeQuery(id+"F0.imprint","INTERSECT",VERTEX,{"derivedFrom":[sQuery(id+"F0.wireOp",EDGE,"E4"),subQ0]}),1.0]])],"derivedFrom":subQ0})])],"isStart":false});}
            var Q9;
            {var subQ0=sQuery(id+"F0.wireOp",EDGE,"E3");var subQ2=makeQuery(id+"F0.imprint","INTERSECT",VERTEX,{"disambiguationData":[OD(1.0)],"derivedFrom":[subQ0,sQuery(id+"F0.wireOp",EDGE,"E28")]});Q9=makeQuery(id+"F1.opExtrude","CAP_EDGE",EDGE,{"disambiguationData":[OSD([subQ0]),TDD([makeQuery(id+"F0.imprint","IMPRINT",EDGE,{"disambiguationData":[TD([[makeQuery(id+"F0.imprint","INTERSECT",VERTEX,{"derivedFrom":[subQ0,sQuery(id+"F0.wireOp",EDGE,"E5")]}),-1.0]])],"derivedFrom":subQ0}),makeQuery(id+"F0.imprint","IMPRINT",EDGE,{"disambiguationData":[TD([[subQ2,-1.0]])],"derivedFrom":subQ0}),makeQuery(id+"F0.imprint","IMPRINT",EDGE,{"disambiguationData":[TD([[makeQuery(id+"F0.imprint","INTERSECT",VERTEX,{"derivedFrom":[subQ0,sQuery(id+"F0.wireOp",EDGE,"E4")]}),1.0]])],"derivedFrom":subQ0})])],"isStart":false});}
            var Q10;
            {var subQ0=sQuery(id+"F0.wireOp",EDGE,"E4");var subQ2=makeQuery(id+"F0.imprint","INTERSECT",VERTEX,{"disambiguationData":[OD(1.0)],"derivedFrom":[subQ0,sQuery(id+"F0.wireOp",EDGE,"E28")]});Q10=makeQuery(id+"F1.opExtrude","CAP_EDGE",EDGE,{"disambiguationData":[OSD([subQ0]),TDD([makeQuery(id+"F0.imprint","IMPRINT",EDGE,{"disambiguationData":[TD([[makeQuery(id+"F0.imprint","INTERSECT",VERTEX,{"derivedFrom":[subQ0,sQuery(id+"F0.wireOp",EDGE,"E5")]}),-1.0]])],"derivedFrom":subQ0}),makeQuery(id+"F0.imprint","IMPRINT",EDGE,{"disambiguationData":[TD([[subQ2,-1.0]])],"derivedFrom":subQ0}),makeQuery(id+"F0.imprint","IMPRINT",EDGE,{"disambiguationData":[TD([[makeQuery(id+"F0.imprint","INTERSECT",VERTEX,{"derivedFrom":[sQuery(id+"F0.wireOp",EDGE,"E3"),subQ0]}),1.0]])],"derivedFrom":subQ0})])],"isStart":false});}
            var Q11;
            {var subQ0=sQuery(id+"F0.wireOp",EDGE,"E5");var subQ2=makeQuery(id+"F0.imprint","INTERSECT",VERTEX,{"disambiguationData":[OD(1.0)],"derivedFrom":[subQ0,sQuery(id+"F0.wireOp",EDGE,"E28")]});Q11=makeQuery(id+"F1.opExtrude","CAP_EDGE",EDGE,{"disambiguationData":[OSD([subQ0]),TDD([makeQuery(id+"F0.imprint","IMPRINT",EDGE,{"disambiguationData":[TD([[makeQuery(id+"F0.imprint","INTERSECT",VERTEX,{"derivedFrom":[sQuery(id+"F0.wireOp",EDGE,"E3"),subQ0]}),-1.0]])],"derivedFrom":subQ0}),makeQuery(id+"F0.imprint","IMPRINT",EDGE,{"disambiguationData":[TD([[subQ2,-1.0]])],"derivedFrom":subQ0}),makeQuery(id+"F0.imprint","IMPRINT",EDGE,{"disambiguationData":[TD([[makeQuery(id+"F0.imprint","INTERSECT",VERTEX,{"derivedFrom":[subQ0,sQuery(id+"F0.wireOp",EDGE,"E6")]}),1.0]])],"derivedFrom":subQ0})])],"isStart":false});}
            var Q12;
            {var subQ0=sQuery(id+"F0.wireOp",EDGE,"E6");var subQ2=makeQuery(id+"F0.imprint","INTERSECT",VERTEX,{"disambiguationData":[OD(0.0)],"derivedFrom":[subQ0,sQuery(id+"F0.wireOp",EDGE,"E27")]});Q12=makeQuery(id+"F1.opExtrude","CAP_EDGE",EDGE,{"disambiguationData":[OSD([subQ0]),TDD([makeQuery(id+"F0.imprint","IMPRINT",EDGE,{"disambiguationData":[TD([[makeQuery(id+"F0.imprint","INTERSECT",VERTEX,{"derivedFrom":[sQuery(id+"F0.wireOp",EDGE,"E5"),subQ0]}),-1.0]])],"derivedFrom":subQ0}),makeQuery(id+"F0.imprint","IMPRINT",EDGE,{"disambiguationData":[TD([[subQ2,-1.0]])],"derivedFrom":subQ0}),makeQuery(id+"F0.imprint","IMPRINT",EDGE,{"disambiguationData":[TD([[makeQuery(id+"F0.imprint","INTERSECT",VERTEX,{"derivedFrom":[sQuery(id+"F0.wireOp",EDGE,"E3"),subQ0]}),1.0]])],"derivedFrom":subQ0})])],"isStart":false});}
            var Q13;
            {var subQ0=sQuery(id+"F0.wireOp",EDGE,"E3");var subQ1=makeQuery(id+"F0.imprint","INTERSECT",VERTEX,{"disambiguationData":[OD(0.0)],"derivedFrom":[subQ0,sQuery(id+"F0.wireOp",EDGE,"E28")]});var subQ2=makeQuery(id+"F0.imprint","INTERSECT",VERTEX,{"disambiguationData":[OD(0.0)],"derivedFrom":[subQ0,sQuery(id+"F0.wireOp",EDGE,"E27")]});Q13=makeQuery(id+"F1.opExtrude","CAP_EDGE",EDGE,{"disambiguationData":[OSD([subQ0]),TDD([makeQuery(id+"F0.imprint","IMPRINT",EDGE,{"disambiguationData":[TD([[makeQuery(id+"F0.imprint","INTERSECT",VERTEX,{"derivedFrom":[sQuery(id+"F0.wireOp",EDGE,"E2"),subQ0]}),-1.0]])],"derivedFrom":subQ0}),makeQuery(id+"F0.imprint","IMPRINT",EDGE,{"disambiguationData":[TD([[subQ2,-1.0]])],"derivedFrom":subQ0}),makeQuery(id+"F0.imprint","IMPRINT",EDGE,{"disambiguationData":[TD([[subQ1,-1.0]])],"derivedFrom":subQ0})])],"isStart":false});}
            var Q14;
            {var subQ0=sQuery(id+"F0.wireOp",EDGE,"E2");var subQ2=makeQuery(id+"F0.imprint","INTERSECT",VERTEX,{"disambiguationData":[OD(1.0)],"derivedFrom":[subQ0,sQuery(id+"F0.wireOp",EDGE,"E28")]});Q14=makeQuery(id+"F1.opExtrude","CAP_EDGE",EDGE,{"disambiguationData":[OSD([subQ0]),TDD([makeQuery(id+"F0.imprint","IMPRINT",EDGE,{"disambiguationData":[TD([[makeQuery(id+"F0.imprint","INTERSECT",VERTEX,{"derivedFrom":[subQ0,sQuery(id+"F0.wireOp",EDGE,"E6")]}),-1.0]])],"derivedFrom":subQ0}),makeQuery(id+"F0.imprint","IMPRINT",EDGE,{"disambiguationData":[TD([[subQ2,-1.0]])],"derivedFrom":subQ0}),makeQuery(id+"F0.imprint","IMPRINT",EDGE,{"disambiguationData":[TD([[makeQuery(id+"F0.imprint","INTERSECT",VERTEX,{"derivedFrom":[subQ0,sQuery(id+"F0.wireOp",EDGE,"E3")]}),1.0]])],"derivedFrom":subQ0})])],"isStart":false});}
            fillet(context, id + "F6", {"entities" : qUnion([Q0, Q1, Q2, Q3, Q4, Q5, Q6, Q7, Q8, Q9, Q10, Q11, Q12, Q13, Q14]), "radius" : 0.5 * mm, "tangentPropagation" : true, "allowEdgeOverflow" : false});
        }
    });
